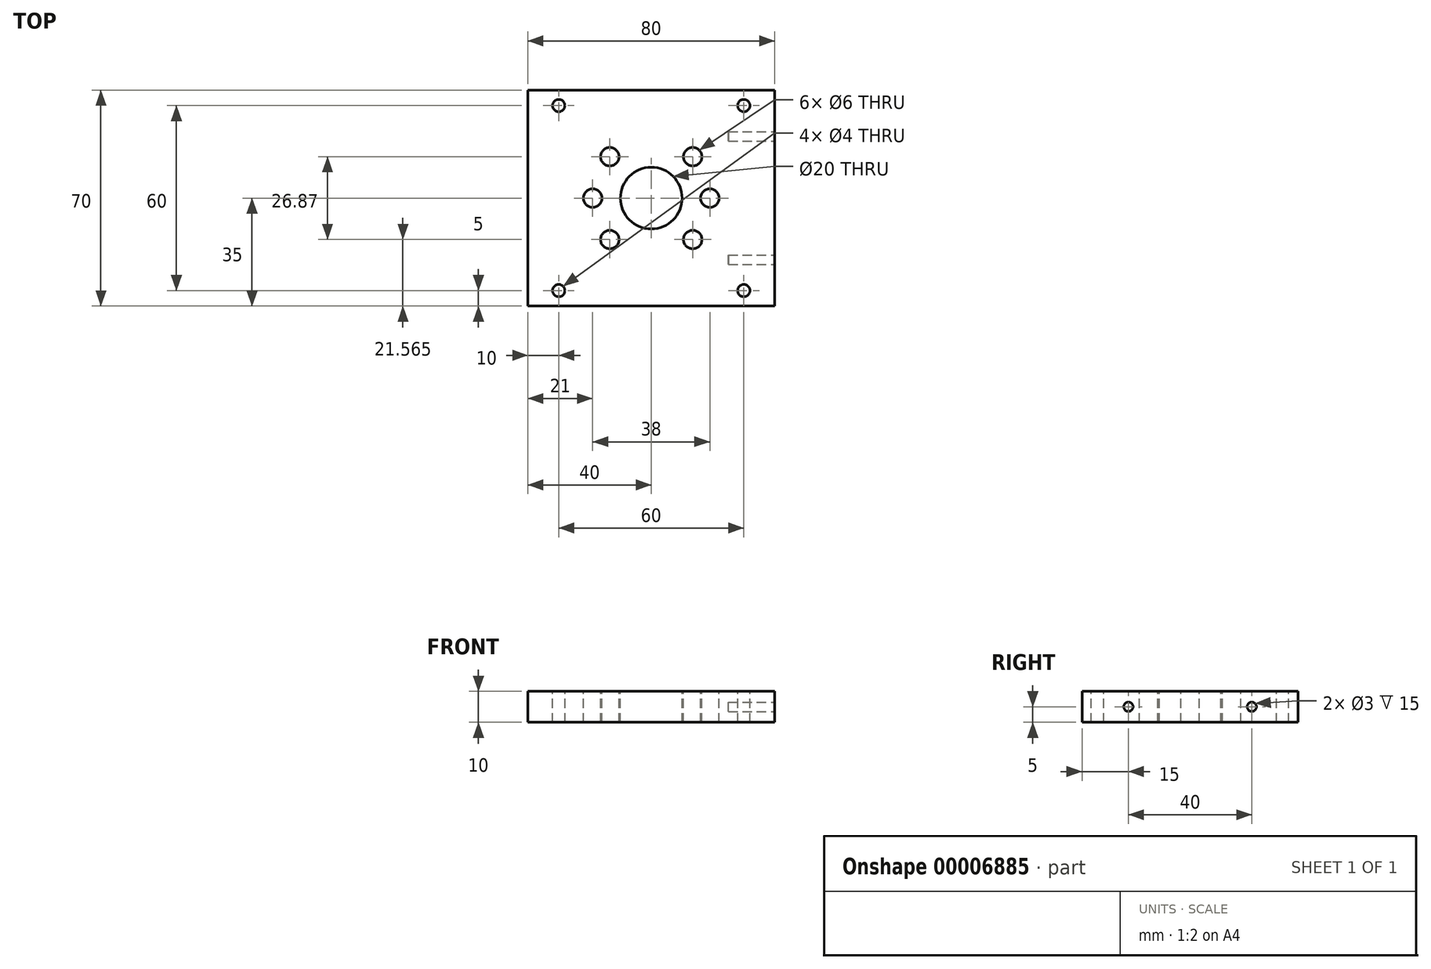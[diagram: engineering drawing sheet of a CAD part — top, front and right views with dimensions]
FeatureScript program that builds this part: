
annotation { "Feature Type Name" : "Feature", "Feature Type Description" : "" }
export const myFeature = defineFeature(function(context is Context, id is Id, definition is map)
    precondition{}
    {
        {
            var Q0;
            Q0=qCreatedBy(makeId("Top.planeOp"),FACE);
            var sketch = newSketch(context, id + "F0", { "sketchPlane" : qUnion([Q0])});
            skLineSegment(sketch, "E0.rect.bottom", {"start": v(40, -35) * mm, "end": v(-40, -35) * mm});
            skLineSegment(sketch, "E0.rect.top", {"start": v(40, 35) * mm, "end": v(-40, 35) * mm});
            skLineSegment(sketch, "E0.rect.left", {"start": v(40, -35) * mm, "end": v(40, 35) * mm});
            skLineSegment(sketch, "E0.rect.right", {"start": v(-40, -35) * mm, "end": v(-40, 35) * mm});
            skPoint(sketch, "E0.rect.middle", {"position": v(0, 0) * mm});
            skSolve(sketch);
        }
        {
            var Q0;
            {var subQ1=sQuery(id+"F0.wireOp",EDGE,"E0.rect.left");Q0=makeQuery(id+"F0.imprint","IMPRINT",FACE,{"disambiguationData":[TD([[makeQuery(id+"F0.imprint","IMPRINT",EDGE,{"derivedFrom":subQ1}),1.0]])]});}
            var Q1;
            {var subQ1=sQuery(id+"F0.wireOp",EDGE,"E0.rect.right");Q1=makeQuery(id+"F0.imprint","IMPRINT",FACE,{"disambiguationData":[TD([[makeQuery(id+"F0.imprint","IMPRINT",EDGE,{"derivedFrom":subQ1}),-1.0]])]});}
            extrude(context, id + "F1", {"entities" : qUnion([Q0, Q1]), "depth" : 10 * mm});
        }
        {
            var Q0;
            Q0=makeQuery(id+"F1.opExtrude","CAP_FACE",FACE,{"disambiguationData":[OSD([sQuery(id+"F0.wireOp",EDGE,"E0.rect.bottom"),sQuery(id+"F0.wireOp",EDGE,"E0.rect.top"),sQuery(id+"F0.wireOp",EDGE,"E0.rect.left"),sQuery(id+"F0.wireOp",EDGE,"E0.rect.right")])],"isStart":false});
            var sketch = newSketch(context, id + "F2", { "sketchPlane" : qUnion([Q0])});
            skLineSegment(sketch, "E1", {"start": v(0, 35) * mm, "end": v(0, -35) * mm, "construction": true});
            skLineSegment(sketch, "E2", {"start": v(20, 0) * mm, "end": v(-40, 0) * mm, "construction": true});
            skCircle(sketch, "E3", {"center": v(0, 0) * mm, "radius": 10 * mm});
            skCircle(sketch, "E4", {"center": v(0, 0) * mm, "radius": 19 * mm, "construction": true});
            skCircle(sketch, "E5", {"center": v(-19, 0) * mm, "radius": 3 * mm});
            skCircle(sketch, "E6", {"center": v(19, 0) * mm, "radius": 3 * mm});
            skLineSegment(sketch, "E7", {"start": v(0, 0) * mm, "end": v(-19.33, 19.33) * mm, "construction": true});
            skLineSegment(sketch, "E8", {"start": v(0, 0) * mm, "end": v(-18.3, -18.3) * mm, "construction": true});
            skLineSegment(sketch, "E9", {"start": v(0, 0) * mm, "end": v(16.8, 16.8) * mm, "construction": true});
            skLineSegment(sketch, "E10", {"start": v(0, 0) * mm, "end": v(17.78, -17.78) * mm, "construction": true});
            skCircle(sketch, "E11", {"center": v(-13.44, 13.44) * mm, "radius": 3 * mm});
            skCircle(sketch, "E12", {"center": v(-13.44, -13.44) * mm, "radius": 3 * mm});
            skCircle(sketch, "E13", {"center": v(13.44, -13.44) * mm, "radius": 3 * mm});
            skCircle(sketch, "E14", {"center": v(13.44, 13.44) * mm, "radius": 3 * mm});
            skSolve(sketch);
        }
        {
            var Q0;
            Q0=makeQuery(id+"F2.imprint","IMPRINT",FACE,{"disambiguationData":[TD([[makeQuery(id+"F2.imprint","IMPRINT",EDGE,{"derivedFrom":sQuery(id+"F2.wireOp",EDGE,"E3")}),1.0]])]});
            var Q1;
            Q1=makeQuery(id+"F2.imprint","IMPRINT",FACE,{"disambiguationData":[TD([[makeQuery(id+"F2.imprint","IMPRINT",EDGE,{"derivedFrom":sQuery(id+"F2.wireOp",EDGE,"E5")}),1.0]])]});
            var Q2;
            Q2=makeQuery(id+"F2.imprint","IMPRINT",FACE,{"disambiguationData":[TD([[makeQuery(id+"F2.imprint","IMPRINT",EDGE,{"derivedFrom":sQuery(id+"F2.wireOp",EDGE,"E6")}),1.0]])]});
            var Q3;
            Q3=makeQuery(id+"F2.imprint","IMPRINT",FACE,{"disambiguationData":[TD([[makeQuery(id+"F2.imprint","IMPRINT",EDGE,{"derivedFrom":sQuery(id+"F2.wireOp",EDGE,"E12")}),1.0]])]});
            var Q4;
            Q4=makeQuery(id+"F2.imprint","IMPRINT",FACE,{"disambiguationData":[TD([[makeQuery(id+"F2.imprint","IMPRINT",EDGE,{"derivedFrom":sQuery(id+"F2.wireOp",EDGE,"E13")}),1.0]])]});
            var Q5;
            Q5=makeQuery(id+"F2.imprint","IMPRINT",FACE,{"disambiguationData":[TD([[makeQuery(id+"F2.imprint","IMPRINT",EDGE,{"derivedFrom":sQuery(id+"F2.wireOp",EDGE,"E14")}),1.0]])]});
            var Q6;
            Q6=makeQuery(id+"F2.imprint","IMPRINT",FACE,{"disambiguationData":[TD([[makeQuery(id+"F2.imprint","IMPRINT",EDGE,{"derivedFrom":sQuery(id+"F2.wireOp",EDGE,"E11")}),1.0]])]});
            extrude(context, id + "F3", {"entities" : qUnion([Q0, Q1, Q2, Q3, Q4, Q5, Q6]), "operationType" : NewBodyOperationType.REMOVE, "oppositeDirection" : true, "depth" : 25 * mm});
        }
        {
            var Q0;
            Q0=makeQuery(id+"F1.opExtrude","CAP_FACE",FACE,{"disambiguationData":[OSD([sQuery(id+"F0.wireOp",EDGE,"E0.rect.bottom"),sQuery(id+"F0.wireOp",EDGE,"E0.rect.top"),sQuery(id+"F0.wireOp",EDGE,"E0.rect.left"),sQuery(id+"F0.wireOp",EDGE,"E0.rect.right")])],"isStart":false});
            var sketch = newSketch(context, id + "F4", { "sketchPlane" : qUnion([Q0])});
            skLineSegment(sketch, "E15", {"start": v(-40, 30) * mm, "end": v(40, 30) * mm, "construction": true});
            skLineSegment(sketch, "E16", {"start": v(-40, -30) * mm, "end": v(40, -30) * mm, "construction": true});
            skCircle(sketch, "E17", {"center": v(-30, 30) * mm, "radius": 2 * mm});
            skCircle(sketch, "E18", {"center": v(30, 30) * mm, "radius": 2 * mm});
            skCircle(sketch, "E19", {"center": v(30, -30) * mm, "radius": 2 * mm});
            skCircle(sketch, "E20", {"center": v(-30, -30) * mm, "radius": 2 * mm});
            skSolve(sketch);
        }
        {
            var Q0;
            Q0=qSketchRegion(id+"F4",true);
            extrude(context, id + "F5", {"entities" : qUnion([Q0]), "operationType" : NewBodyOperationType.REMOVE, "endBound" : BoundingType.THROUGH_ALL, "oppositeDirection" : true, "depth" : 25 * mm});
        }
        {
            var Q0;
            Q0=makeQuery(id+"F1.opExtrude","SWEPT_FACE",FACE,{"disambiguationData":[OSD([sQuery(id+"F0.wireOp",EDGE,"E0.rect.left")])]});
            var sketch = newSketch(context, id + "F6", { "sketchPlane" : qUnion([Q0])});
            skLineSegment(sketch, "E21", {"start": v(-35, 5) * mm, "end": v(35, 5) * mm, "construction": true});
            skCircle(sketch, "E22", {"center": v(-20, 5) * mm, "radius": 1.5 * mm});
            skCircle(sketch, "E23", {"center": v(20, 5) * mm, "radius": 1.5 * mm});
            skSolve(sketch);
        }
        {
            var Q0;
            Q0=qSketchRegion(id+"F6",true);
            extrude(context, id + "F7", {"entities" : qUnion([Q0]), "operationType" : NewBodyOperationType.REMOVE, "oppositeDirection" : true, "depth" : (15) * mm});
        }
    });
